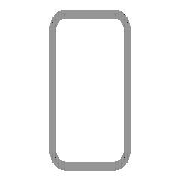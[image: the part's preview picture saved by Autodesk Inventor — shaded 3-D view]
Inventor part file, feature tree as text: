
AUTODESK INVENTOR PART (.ipt)
format: ipt  version: 2025 (Build 290162010, 162A)  size: 133,632 bytes
history: native  units: mm (DEFAULTED — no unit token found)
features: other x4, sketch x1, plane x1
ambient origin geometry x8: Origin, YZ Plane, XZ Plane, XY Plane, X Axis, Y Axis, Z Axis, Center Point
bodies: Solid1 (feature_tree), Body (feature_tree)
feature tree (6):
  parser-record x1  (decoder bookkeeping rows leaked as tree rows — omitted from the tree; the rows remain in map.json)
  other  "Driven Length"
  other  "Start Plane"
  other  "End Plane"
  sketch  "Sketch3"  dims[d3=760.0mm d4=0.0mm d7=4.0mm d9=20.0mm d11=40.0mm d12=2.0mm d13=20.0mm d14=780.0mm d15=10.0mm d16=20.0mm d17=90.0deg d18=760.0mm]
  plane  "Work Plane3"
